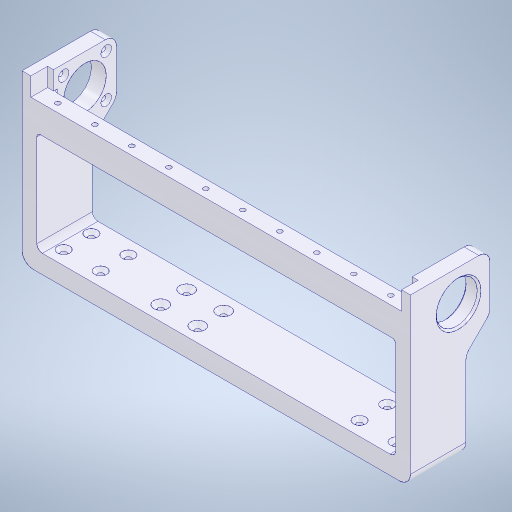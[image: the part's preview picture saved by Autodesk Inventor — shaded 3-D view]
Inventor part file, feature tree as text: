
AUTODESK INVENTOR PART (.ipt)
format: ipt  version: 2024.1 (Build 281209000, 209)  size: 465,920 bytes
history: native  units: in
note: dims shown in document units (in); Inventor stores cm internally (conversion verified against a paired STEP export)
features: extrude x10, sketch x10, chamfer x5, fillet x4
ambient origin geometry x8: Origin, YZ Plane, XZ Plane, XY Plane, X Axis, Y Axis, Z Axis, Center Point
bodies: Solid1 (feature_tree)
feature tree (29):
  extrude  "Extrusion1"  Depth=3.5433in
  extrude  "Extrusion2"  Depth=0.315in
  extrude  "Extrusion3"  Depth=0.3937in
  chamfer  "Chamfer1"  Distance=1.1811in
  extrude  "Extrusion9"  Depth=0.1181in
  chamfer  "Chamfer4"  Distance=0.2953in
  extrude  "Extrusion12"  Depth=0.0787in
  extrude  "Extrusion13"  Depth=0.0787in
  fillet  "Fillet3"  Radius=0.2953in
  extrude  "Extrusion14"  Depth=0.0787in
  extrude  "Extrusion15"  Depth=0.0787in
  chamfer  "Chamfer9"  Distance=0.2756in
  fillet  "Fillet4"  Radius=0.7874in
  fillet  "Fillet5"  Radius=0.7874in
  fillet  "Fillet6"  Radius=0.2756in
  extrude  "Extrusion17"  Depth=0.5906in
  chamfer  "Chamfer10"  Distance=0.5906in
  extrude  "Extrusion18"  Depth=0.5906in
  chamfer  "Chamfer11"  Distance=0.5906in
  sketch  "Sketch1"  dims[d0=8.2677in d1=3.5433in]
  sketch  "Sketch2"  dims[d2=1.1811in d3=0.0in d4=0.315in]
  sketch  "Sketch3"  dims[d5=0.315in d6=0.3937in d7=1.1811in d8=0.0in]
  sketch  "Sketch9"  dims[d9=0.1181in d10=0.1181in]
  sketch  "Sketch12"  dims[d11=0.1181in]
  sketch  "Sketch13"  dims[d12=0.1181in]
  sketch  "Sketch14"  dims[d13=0.1181in]
  sketch  "Sketch15"  dims[d14=0.1181in]
  sketch  "Sketch17"  dims[d15=0.1181in]
  sketch  "Sketch18"  dims[d16=0.1181in d18=0.2953in d19=0.2953in d20=0.2953in d21=0.2953in d22=0.7874in d23=0.7874in d24=0.2756in d25=0.7874in d26=0.7874in d27=0.2756in d28=0.5906in d29=0.5906in d30=0.5906in d31=0.5906in d33=5.5118in d34=5.5118in d35=1.1811in d36=0.0in d37=0.0709in d38=0.125in d39=45.0deg d74=1.1811in d75=1.1811in d76=0.5118in d77=0.0in d78=0.5118in d79=0.0787in d80=45.0deg d90=0.315in d97=0.3543in d98=0.5906in d99=0.3937in d100=7.6378in d101=0.0in d102=0.9055in d103=0.6693in d104=0.6693in d105=7.9528in d106=0.0in d107=0.0787in d108=0.3543in d109=0.126in d110=0.126in d111=0.3937in d112=0.0in d116=0.3976in d117=0.1772in d118=3.937in d120=0.7874in d121=0.3937in d123=0.3937in d125=0.5906in d126=0.0in d127=0.1024in d128=0.0984in d129=0.0984in d130=0.0984in d131=0.0984in d132=0.4528in d133=0.4528in d134=0.4528in d135=0.4528in d136=0.4528in d137=0.4528in d138=0.4528in d139=0.4528in d149=0.063in d150=0.0787in d151=45.0deg d152=0.1181in d153=0.2362in d154=0.2362in d155=0.1181in d156=0.1181in d157=0.1181in d158=0.1181in d159=0.315in d160=0.315in d161=0.315in d162=0.315in d163=0.7874in d164=0.7874in d165=2.3228in d166=2.3228in d167=0.3937in d168=0.0in d169=0.0906in d170=0.0787in d171=45.0deg d172=0.874in d173=0.0in d174=0.0in d175=0.0394in d176=0.0787in d177=45.0deg]
